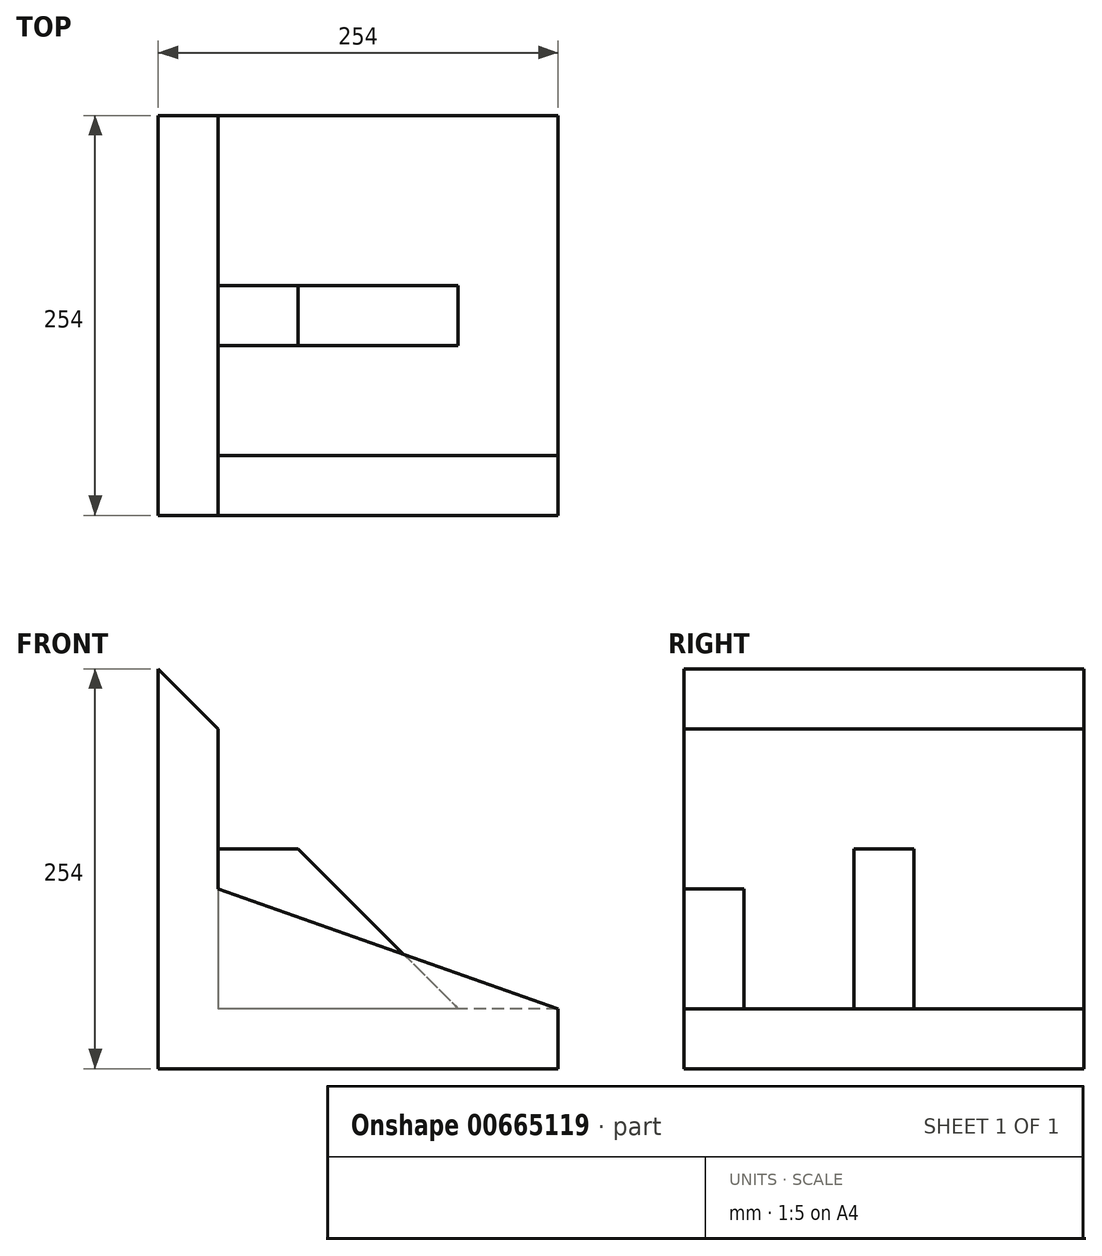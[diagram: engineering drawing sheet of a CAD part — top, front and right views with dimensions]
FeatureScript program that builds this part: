
annotation { "Feature Type Name" : "Feature", "Feature Type Description" : "" }
export const myFeature = defineFeature(function(context is Context, id is Id, definition is map)
    precondition{}
    {
        {
            var Q0;
            Q0=qCreatedBy(makeId("Front.planeOp"),FACE);
            var sketch = newSketch(context, id + "F0", { "sketchPlane" : qUnion([Q0])});
            skLineSegment(sketch, "E0", {"start": v(0, 0) * mm, "end": v(254, 0) * mm});
            skLineSegment(sketch, "E1", {"start": v(0, 0) * mm, "end": v(0, 254) * mm});
            skLineSegment(sketch, "E2", {"start": v(254, 0) * mm, "end": v(254, 38.1) * mm});
            skLineSegment(sketch, "E3", {"start": v(254, 38.1) * mm, "end": v(38.1, 38.1) * mm});
            skLineSegment(sketch, "E4", {"start": v(38.1, 215.9) * mm, "end": v(0, 254) * mm});
            skLineSegment(sketch, "E5", {"start": v(38.1, 215.9) * mm, "end": v(38.1, 38.1) * mm});
            skLineSegment(sketch, "E6", {"start": v(38.1, 38.1) * mm, "end": v(38.1, 139.7) * mm});
            skLineSegment(sketch, "E7", {"start": v(38.1, 139.7) * mm, "end": v(88.9, 139.7) * mm});
            skLineSegment(sketch, "E8", {"start": v(88.9, 139.7) * mm, "end": v(190.5, 38.1) * mm});
            skSolve(sketch);
        }
        {
            var Q0;
            Q0=makeQuery(id+"F0.imprint","IMPRINT",FACE,{"disambiguationData":[TD([[makeQuery(id+"F0.imprint","IMPRINT",EDGE,{"derivedFrom":sQuery(id+"F0.wireOp",EDGE,"E0")}),1.0]])]});
            extrude(context, id + "F1", {"entities" : qUnion([Q0]), "endBound" : BoundingType.SYMMETRIC, "depth" : 254 * mm, "offsetDistance" : 25.4 * mm});
        }
        {
            var Q0;
            Q0=makeQuery(id+"F1.opExtrude","CAP_FACE",FACE,{"disambiguationData":[OSD([sQuery(id+"F0.wireOp",EDGE,"E0"),sQuery(id+"F0.wireOp",EDGE,"E1"),sQuery(id+"F0.wireOp",EDGE,"E2"),sQuery(id+"F0.wireOp",EDGE,"E3"),sQuery(id+"F0.wireOp",EDGE,"E4"),sQuery(id+"F0.wireOp",EDGE,"E5")])],"isStart":false});
            var sketch = newSketch(context, id + "F2", { "sketchPlane" : qUnion([Q0])});
            skLineSegment(sketch, "E9", {"start": v(38.1, 114.3) * mm, "end": v(254, 38.1) * mm});
            skSolve(sketch);
        }
        {
            var Q0;
            {var subQ0=sQuery(id+"F2.wireOp",EDGE,"E9");Q0=makeQuery(id+"F2.imprint","IMPRINT",FACE,{"disambiguationData":[TD([[makeQuery(id+"F2.imprint","IMPRINT",EDGE,{"derivedFrom":subQ0}),-1.0]])]});}
            extrude(context, id + "F3", {"entities" : qUnion([Q0]), "operationType" : NewBodyOperationType.ADD, "oppositeDirection" : true, "depth" : 38.1 * mm, "offsetDistance" : 25.4 * mm});
        }
        {
            var Q0;
            Q0 = qSketchRegion(id + "F0", true);
            extrude(context, id + "F4", {"entities" : qUnion([Q0]), "operationType" : NewBodyOperationType.ADD, "endBound" : BoundingType.SYMMETRIC, "depth" : 38.1 * mm, "offsetDistance" : 25.4 * mm});
        }
    });
